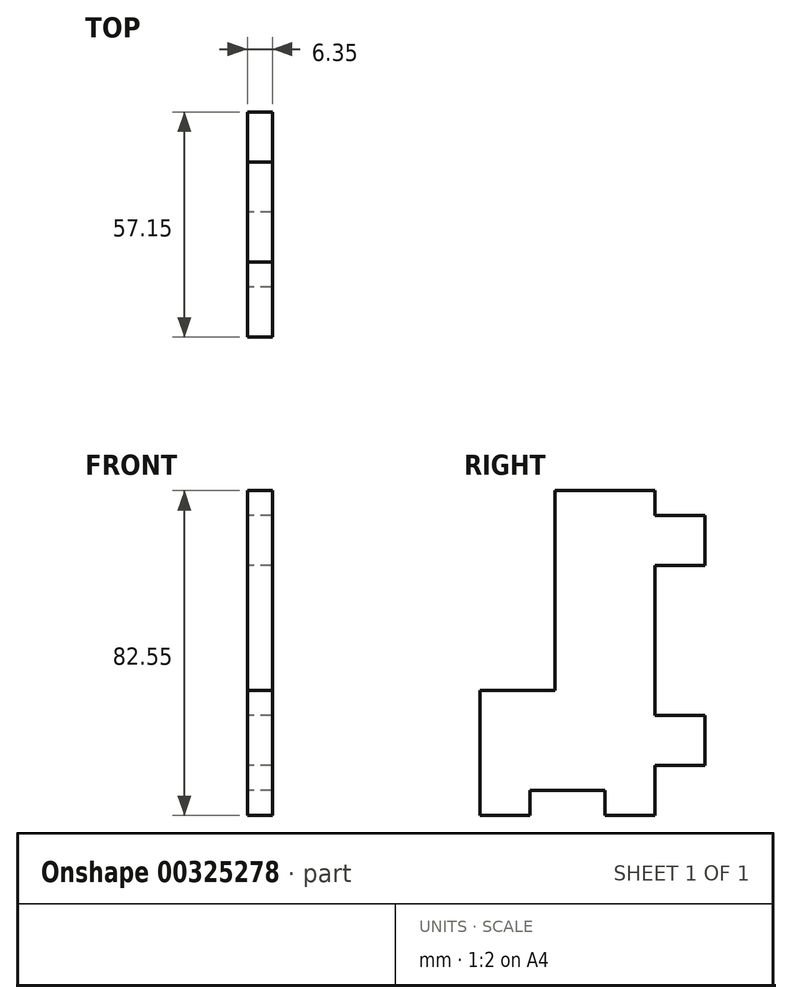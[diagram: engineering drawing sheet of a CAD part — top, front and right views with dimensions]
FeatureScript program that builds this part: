
annotation { "Feature Type Name" : "Feature", "Feature Type Description" : "" }
export const myFeature = defineFeature(function(context is Context, id is Id, definition is map)
    precondition{}
    {
        {
            var Q0;
            Q0=qCreatedBy(makeId("Right.planeOp"),FACE);
            var sketch = newSketch(context, id + "F0", { "sketchPlane" : qUnion([Q0])});
            skLineSegment(sketch, "E0", {"start": v(0, 0) * mm, "end": v(0, 0) * mm});
            skLineSegment(sketch, "E1", {"start": v(0, 0) * mm, "end": v(0, -6.35) * mm});
            skLineSegment(sketch, "E2", {"start": v(0, -6.35) * mm, "end": v(12.7, -6.35) * mm});
            skLineSegment(sketch, "E3", {"start": v(12.7, -6.35) * mm, "end": v(12.7, 0) * mm});
            skLineSegment(sketch, "E4", {"start": v(12.7, 0) * mm, "end": v(31.75, 0) * mm});
            skLineSegment(sketch, "E5", {"start": v(31.75, 0) * mm, "end": v(31.75, -6.35) * mm});
            skLineSegment(sketch, "E6", {"start": v(31.75, -6.35) * mm, "end": v(44.45, -6.35) * mm});
            skLineSegment(sketch, "E7", {"start": v(44.45, 76.2) * mm, "end": v(19.05, 76.2) * mm});
            skLineSegment(sketch, "E8", {"start": v(19.05, 76.2) * mm, "end": v(19.05, 25.4) * mm});
            skLineSegment(sketch, "E9", {"start": v(19.05, 25.4) * mm, "end": v(0, 25.4) * mm});
            skLineSegment(sketch, "E10", {"start": v(0, 25.4) * mm, "end": v(0, 0) * mm});
            skLineSegment(sketch, "E11", {"start": v(44.45, 76.2) * mm, "end": v(44.45, 69.85) * mm});
            skLineSegment(sketch, "E12", {"start": v(44.45, 69.85) * mm, "end": v(57.15, 69.85) * mm});
            skLineSegment(sketch, "E13", {"start": v(57.15, 69.85) * mm, "end": v(57.15, 57.15) * mm});
            skLineSegment(sketch, "E14", {"start": v(57.15, 57.15) * mm, "end": v(44.45, 57.15) * mm});
            skLineSegment(sketch, "E15", {"start": v(44.45, 57.15) * mm, "end": v(44.45, 19.05) * mm});
            skLineSegment(sketch, "E16", {"start": v(44.45, 19.05) * mm, "end": v(57.15, 19.05) * mm});
            skLineSegment(sketch, "E17", {"start": v(57.15, 19.05) * mm, "end": v(57.15, 6.35) * mm});
            skLineSegment(sketch, "E18", {"start": v(57.15, 6.35) * mm, "end": v(44.45, 6.35) * mm});
            skLineSegment(sketch, "E19", {"start": v(44.45, 6.35) * mm, "end": v(44.45, -6.35) * mm});
            skSolve(sketch);
        }
        {
            var Q0;
            Q0=makeQuery(id+"F0.imprint","IMPRINT",FACE,{"disambiguationData":[TD([[makeQuery(id+"F0.imprint","IMPRINT",EDGE,{"derivedFrom":sQuery(id+"F0.wireOp",EDGE,"E1")}),1.0]])]});
            extrude(context, id + "F1", {"entities" : qUnion([Q0]), "depth" : 6.35 * mm});
        }
    });
